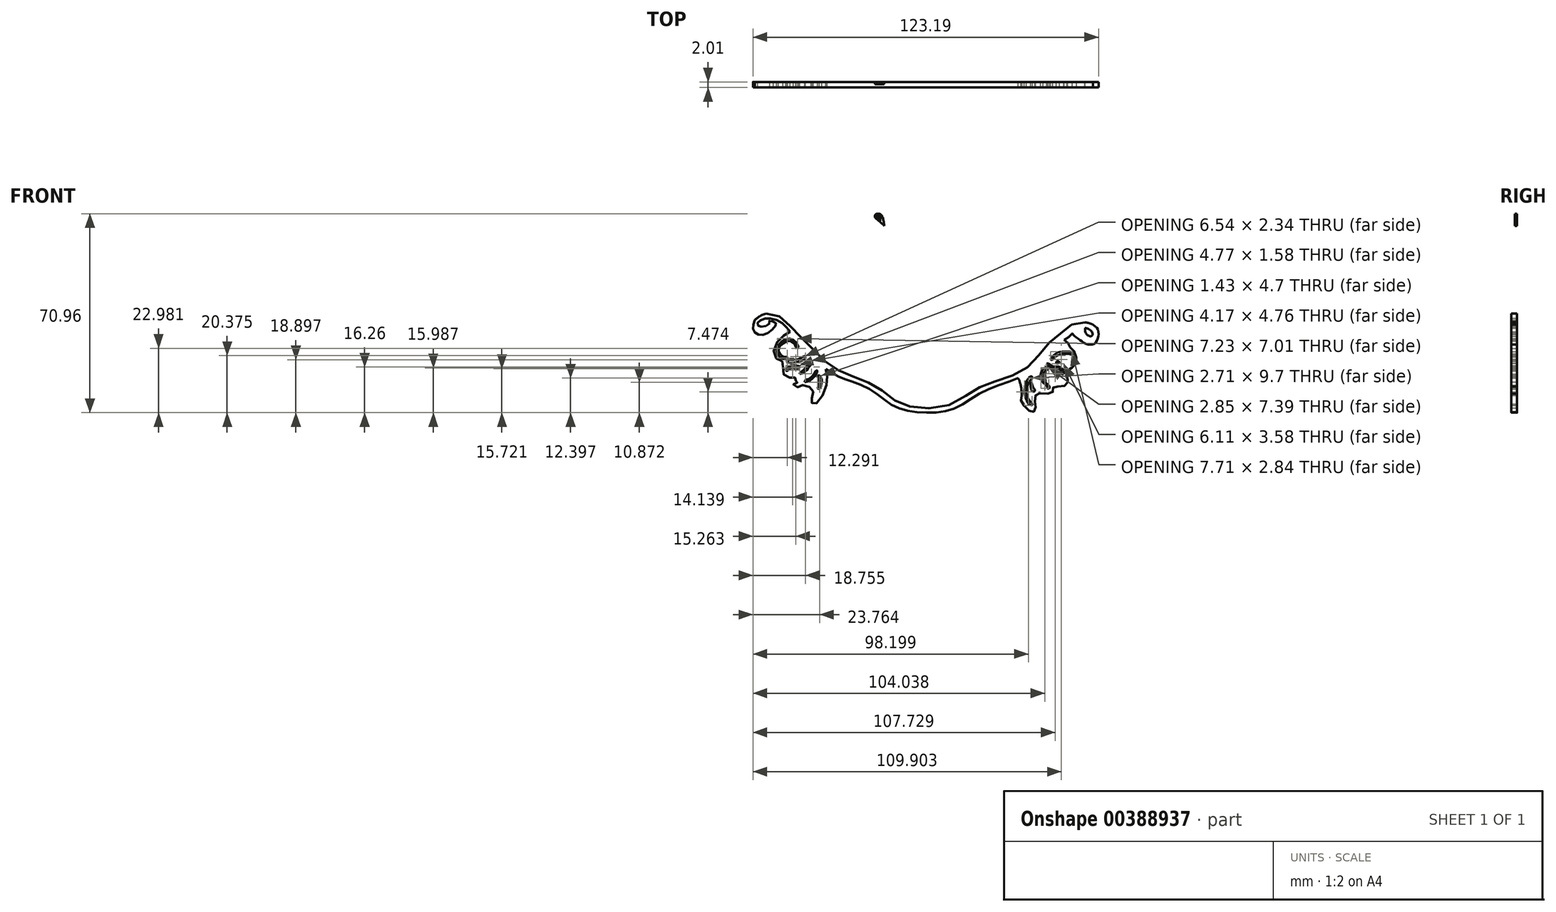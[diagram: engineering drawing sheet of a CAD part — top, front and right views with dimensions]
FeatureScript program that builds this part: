
annotation { "Feature Type Name" : "Feature", "Feature Type Description" : "" }
export const myFeature = defineFeature(function(context is Context, id is Id, definition is map)
    precondition{}
    {
        {
            var Q0;
            Q0=qCreatedBy(makeId("Front.planeOp"),FACE);
            var sketch = newSketch(context, id + "F0", { "sketchPlane" : qUnion([Q0])});
            skFitSpline(sketch, "E0", {"points": [v(-19.06, -22.64) * mm, v(-20.05, -23.28) * mm, v(-21.17, -24.66) * mm, v(-21.14, -26.1) * mm, v(-20.24, -26.68) * mm, v(-20.05, -26.78) * mm, v(-20.05, -28.02) * mm, v(-19.7, -28.73) * mm, v(-18.72, -28.96) * mm, v(-18.37, -28.92) * mm, v(-18.26, -29) * mm, v(-18.28, -29.36) * mm, v(-18, -29.5) * mm, v(-18.05, -29.57) * mm, v(-18.53, -29.7) * mm, v(-18.56, -30.03) * mm, v(-18.01, -30.22) * mm, v(-17.5, -29.95) * mm, v(-16.56, -30.12) * mm, v(-15.97, -30.64) * mm, v(-16, -31.53) * mm, v(-16.2, -32.1) * mm, v(-16, -32.47) * mm, v(-15.44, -32.4) * mm, v(-14.27, -30.56) * mm, v(-14, -28.79) * mm, v(-14.2, -27.76) * mm], "startDerivative": vector(-19.78, -11.14) * mm, "endDerivative": vector(-5.37, 21.05) * mm});
            skFitSpline(sketch, "E1", {"points": [v(-14.2, -27.76) * mm, v(-16.2, -25.63) * mm, v(-18.24, -23.45) * mm, v(-19.06, -22.64) * mm, v(-20.05, -21.54) * mm, v(-21.57, -20.88) * mm, v(-22.78, -20.92) * mm, v(-23.48, -21.37) * mm, v(-23.5, -21.72) * mm, v(-23.2, -21.93) * mm, v(-22.36, -21.87) * mm, v(-21.9, -21.51) * mm, v(-21.88, -21.16) * mm, v(-21.32, -21.3) * mm, v(-20.95, -21.55) * mm, v(-21.14, -21.94) * mm, v(-22.16, -22.82) * mm, v(-23.15, -23.1) * mm, v(-23.83, -22.82) * mm, v(-24.15, -22.22) * mm, v(-23.98, -21.37) * mm, v(-23.86, -20.47) * mm, v(-24.2, -19.7) * mm, v(-24.66, -19.2) * mm, v(-24.75, -18.9) * mm, v(-24.3, -18.34) * mm, v(-23.08, -17.57) * mm, v(-21.55, -17.56) * mm, v(-19.9, -18.28) * mm, v(-18.3, -19.4) * mm, v(-16.67, -20.86) * mm, v(-15.6, -22.07) * mm, v(-14.1, -23.87) * mm, v(-12.14, -25.56) * mm, v(-10.39, -26.53) * mm, v(-8.44, -27.2) * mm, v(-5.99, -28.28) * mm, v(-4.2, -29.6) * mm, v(-2.28, -30.28) * mm, v(-0.2, -30.3) * mm, v(2.58, -29.54) * mm, v(5.26, -28.2) * mm, v(8.77, -26.78) * mm, v(9.41, -26.65) * mm, v(11.78, -25.36) * mm, v(14.45, -23.04) * mm, v(14.48, -22.64) * mm, v(14.42, -21.53) * mm, v(15.26, -19.72) * mm, v(16.52, -18.65) * mm, v(17.53, -18.57) * mm, v(18.11, -18.9) * mm, v(18.07, -19.55) * mm, v(18, -19.69) * mm, v(18.83, -19.1) * mm, v(20.97, -18.63) * mm, v(22.66, -19.01) * mm, v(23.52, -19.67) * mm, v(23.84, -20.62) * mm, v(23.52, -21.03) * mm, v(23.13, -20.85) * mm, v(22.93, -21.03) * mm, v(22.8, -21.42) * mm, v(22.3, -21.67) * mm, v(22.84, -22.17) * mm, v(23, -23.35) * mm, v(22.47, -24.3) * mm, v(21.3, -24.28) * mm, v(20.25, -23.57) * mm, v(19.46, -22.82) * mm, v(20.12, -22.18) * mm, v(21.2, -22.13) * mm, v(21.96, -22.45) * mm, v(22.24, -23) * mm, v(21.92, -23.27) * mm, v(21.32, -22.82) * mm, v(21.2, -22.14) * mm], "startDerivative": vector(-92.8, 97.5) * mm, "endDerivative": vector(-0.23, 68.35) * mm});
            skLineSegment(sketch, "E2", {"start": v(21.2, -22.14) * mm, "end": v(21.2, -22.13) * mm});
            skFitSpline(sketch, "E3", {"points": [v(19.46, -22.82) * mm, v(19.39, -22.99) * mm, v(18.36, -23.75) * mm, v(17.08, -24.5) * mm, v(16.07, -25.85) * mm, v(13.94, -27.93) * mm, v(11.12, -29.36) * mm, v(7.1, -30.91) * mm, v(3.97, -32.85) * mm, v(0.94, -33.67) * mm, v(-2.51, -33.52) * mm, v(-5.24, -32.64) * mm, v(-7.54, -30.9) * mm, v(-10.64, -29.44) * mm, v(-12.46, -28.79) * mm, v(-14.2, -27.76) * mm], "startDerivative": vector(-1.63, -7.8) * mm, "endDerivative": vector(-28.62, 18.77) * mm});
            skFitSpline(sketch, "E4", {"points": [v(12.8, -28.63) * mm, v(12.8, -30.04) * mm, v(12.55, -31.33) * mm, v(12.47, -32.12) * mm, v(13.23, -33.09) * mm, v(14.06, -33.65) * mm, v(14.44, -33.2) * mm, v(14.39, -32.3) * mm, v(14.47, -31.3) * mm, v(15, -31.06) * mm, v(16.65, -31.04) * mm, v(16.82, -30.58) * mm, v(16.9, -30.2) * mm, v(18.08, -30.12) * mm, v(18.76, -29.77) * mm, v(18.78, -28.63) * mm, v(18.78, -27.94) * mm, v(19.62, -27.42) * mm, v(20.03, -26.64) * mm, v(19.84, -25.5) * mm, v(19.22, -24.8) * mm, v(18.95, -24.27) * mm, v(18.36, -23.75) * mm], "startDerivative": vector(-7.26, -31.01) * mm, "endDerivative": vector(-16.3, 11.39) * mm});
            skFitSpline(sketch, "E5", {"points": [v(-14.2, -27.76) * mm, v(-16.2, -25.63) * mm, v(-18.24, -23.45) * mm, v(-19.06, -22.64) * mm, v(-20.05, -21.54) * mm, v(-21.57, -20.88) * mm, v(-22.78, -20.92) * mm, v(-23.48, -21.37) * mm, v(-23.5, -21.72) * mm, v(-23.2, -21.93) * mm, v(-22.36, -21.87) * mm, v(-21.9, -21.51) * mm, v(-21.88, -21.16) * mm, v(-21.32, -21.3) * mm, v(-20.95, -21.55) * mm, v(-21.14, -21.94) * mm, v(-22.16, -22.82) * mm, v(-23.15, -23.1) * mm, v(-23.83, -22.82) * mm, v(-24.15, -22.22) * mm, v(-23.98, -21.37) * mm, v(-23.86, -20.47) * mm, v(-24.2, -19.7) * mm, v(-24.66, -19.2) * mm, v(-24.75, -18.9) * mm, v(-24.3, -18.34) * mm, v(-23.08, -17.57) * mm, v(-21.55, -17.56) * mm, v(-19.9, -18.28) * mm, v(-18.3, -19.4) * mm, v(-16.67, -20.86) * mm, v(-15.6, -22.07) * mm, v(-14.1, -23.87) * mm, v(-12.14, -25.56) * mm, v(-10.39, -26.53) * mm, v(-8.44, -27.2) * mm, v(-5.99, -28.28) * mm, v(-4.2, -29.6) * mm, v(-2.28, -30.28) * mm, v(-0.2, -30.3) * mm, v(2.58, -29.54) * mm, v(5.26, -28.2) * mm, v(8.77, -26.78) * mm, v(9.41, -26.65) * mm, v(11.78, -25.36) * mm, v(14.45, -23.04) * mm, v(14.48, -22.64) * mm, v(14.42, -21.53) * mm, v(15.26, -19.72) * mm, v(16.52, -18.65) * mm, v(17.53, -18.57) * mm, v(18.11, -18.9) * mm, v(18.07, -19.55) * mm, v(18, -19.69) * mm, v(18.83, -19.1) * mm, v(20.97, -18.63) * mm, v(22.66, -19.01) * mm, v(23.52, -19.67) * mm, v(23.84, -20.62) * mm, v(23.52, -21.03) * mm, v(23.13, -20.85) * mm, v(22.93, -21.03) * mm, v(22.8, -21.42) * mm, v(22.3, -21.67) * mm, v(22.84, -22.17) * mm, v(23, -23.35) * mm, v(22.47, -24.3) * mm, v(21.3, -24.28) * mm, v(20.25, -23.57) * mm, v(19.46, -22.82) * mm, v(20.12, -22.18) * mm, v(21.2, -22.13) * mm, v(21.96, -22.45) * mm, v(22.24, -23) * mm, v(21.92, -23.27) * mm, v(21.32, -22.82) * mm, v(21.2, -22.14) * mm], "startDerivative": vector(-92.8, 97.5) * mm, "endDerivative": vector(-0.23, 68.35) * mm});
            skFitSpline(sketch, "E6", {"points": [v(-19.05, -18.84) * mm, v(-19.5, -18.2) * mm, v(-19.43, -17.39) * mm, v(-18.26, -17.03) * mm, v(-17.3, -17.47) * mm, v(-16.59, -19) * mm, v(-16.24, -21.32) * mm], "startDerivative": vector(-4.14, 4.31) * mm, "endDerivative": vector(1.1, -10.49) * mm});
            skFitSpline(sketch, "E7", {"points": [v(-19.52, -26.08) * mm, v(-19.84, -26.12) * mm, v(-20.45, -25.73) * mm, v(-20.62, -24.86) * mm, v(-19.83, -24.09) * mm, v(-19.21, -23.9) * mm, v(-18.43, -24.31) * mm, v(-18.22, -24.88) * mm, v(-17.97, -24.91) * mm, v(-17.96, -24.62) * mm, v(-18.36, -24) * mm, v(-19.05, -23.59) * mm, v(-19.74, -23.69) * mm, v(-20.73, -24.56) * mm, v(-20.88, -25.38) * mm, v(-20.47, -26.16) * mm, v(-19.75, -26.41) * mm, v(-19.4, -26.3) * mm, v(-19.52, -26.08) * mm]});
            skFitSpline(sketch, "E8", {"points": [v(-19.55, -26.72) * mm, v(-19.34, -26.54) * mm, v(-18.47, -26.48) * mm, v(-17.55, -26.2) * mm, v(-17.08, -26) * mm, v(-17.01, -26.3) * mm, v(-18.24, -26.82) * mm, v(-19.24, -26.9) * mm, v(-19.55, -26.72) * mm]});
            skFitSpline(sketch, "E9", {"points": [v(-19.65, -27.89) * mm, v(-19.49, -27.99) * mm, v(-19.17, -27.73) * mm, v(-18.62, -27.6) * mm, v(-18.01, -27.68) * mm, v(-17.79, -27.48) * mm, v(-17.94, -27.3) * mm, v(-19.05, -27.33) * mm, v(-19.48, -27.6) * mm, v(-19.65, -27.89) * mm]});
            skFitSpline(sketch, "E10", {"points": [v(-17.76, -28.4) * mm, v(-17.68, -28.21) * mm, v(-17.17, -27.82) * mm, v(-16.63, -27.06) * mm, v(-16.24, -26.57) * mm, v(-16.07, -26.72) * mm, v(-16.55, -27.58) * mm, v(-17.22, -28.25) * mm, v(-17.76, -28.4) * mm]});
            skFitSpline(sketch, "E11", {"points": [v(-17.05, -29.5) * mm, v(-17.02, -29.33) * mm, v(-16.45, -29.05) * mm, v(-15.89, -28.5) * mm, v(-15.57, -28.01) * mm, v(-15.36, -27.96) * mm, v(-15.45, -28.3) * mm, v(-16.03, -29.05) * mm, v(-16.71, -29.46) * mm, v(-17.05, -29.5) * mm]});
            skFitSpline(sketch, "E12", {"points": [v(-15.32, -28.73) * mm, v(-15.14, -29.09) * mm, v(-15.1, -29.6) * mm, v(-15.25, -30.16) * mm, v(-15.3, -30.4) * mm, v(-15.08, -30.43) * mm, v(-14.74, -29.55) * mm, v(-14.93, -28.73) * mm, v(-15.17, -28.61) * mm, v(-15.32, -28.73) * mm]});
            skFitSpline(sketch, "E13", {"points": [v(-18.46, -17.58) * mm, v(-18.7, -17.6) * mm, v(-18.73, -17.92) * mm, v(-18.26, -17.98) * mm, v(-17.78, -17.9) * mm, v(-17.4, -18.3) * mm, v(-17.53, -18.75) * mm, v(-17.88, -18.95) * mm, v(-17.56, -19.27) * mm, v(-17.57, -19.55) * mm, v(-17.96, -19.36) * mm, v(-18.33, -18.9) * mm, v(-18.05, -18.5) * mm, v(-17.62, -18.4) * mm, v(-17.82, -18.14) * mm, v(-18.34, -18.2) * mm, v(-18.89, -18.1) * mm, v(-19.05, -17.65) * mm, v(-18.66, -17.32) * mm, v(-18.46, -17.58) * mm]});
            skLineSegment(sketch, "E14", {"start": v(18, -19.69) * mm, "end": v(18, -19.69) * mm});
            skFitSpline(sketch, "E15", {"points": [v(13.83, -32.7) * mm, v(13.12, -31.76) * mm, v(12.93, -30.48) * mm, v(13.29, -29.28) * mm, v(13.9, -28.73) * mm, v(14.01, -28.93) * mm, v(13.6, -29.47) * mm, v(13.23, -30.5) * mm, v(13.3, -31.44) * mm, v(13.83, -32.3) * mm, v(14.04, -32.57) * mm, v(13.83, -32.7) * mm]});
            skFitSpline(sketch, "E16", {"points": [v(13.83, -29.51) * mm, v(14.04, -30.01) * mm, v(14.2, -30.37) * mm, v(14.4, -30.67) * mm, v(14.14, -30.85) * mm, v(13.8, -30.24) * mm, v(13.83, -29.51) * mm]});
            skFitSpline(sketch, "E17", {"points": [v(15.63, -27.68) * mm, v(15.89, -27.43) * mm, v(16.08, -27.45) * mm, v(16.14, -27.73) * mm, v(15.77, -28) * mm, v(15.5, -28.55) * mm, v(15.58, -29.26) * mm, v(16.14, -29.88) * mm, v(16.39, -30.25) * mm, v(16.24, -30.46) * mm, v(16.04, -30.16) * mm, v(15.4, -29.5) * mm, v(15.17, -28.81) * mm, v(15.27, -28.04) * mm, v(15.63, -27.68) * mm]});
            skFitSpline(sketch, "E18", {"points": [v(15.96, -27) * mm, v(16.55, -27.56) * mm, v(17.47, -27.7) * mm, v(17.84, -27.87) * mm, v(17.9, -28.19) * mm, v(18.02, -28.43) * mm, v(18.28, -28.4) * mm, v(18.25, -27.99) * mm, v(17.82, -27.49) * mm, v(17.21, -27.4) * mm, v(16.72, -27.35) * mm, v(16.27, -27.02) * mm, v(15.96, -27) * mm]});
            skFitSpline(sketch, "E19", {"points": [v(16.48, -26.45) * mm, v(16.71, -26.5) * mm, v(17, -26.18) * mm, v(17.64, -25.79) * mm, v(18.56, -25.67) * mm, v(19.17, -25.74) * mm, v(19.45, -25.78) * mm, v(19.35, -25.48) * mm, v(18.57, -25.36) * mm, v(17.74, -25.4) * mm, v(17.09, -25.75) * mm, v(16.48, -26.45) * mm]});
            skFitSpline(sketch, "E20", {"points": [v(17.33, -26.7) * mm, v(17.59, -26.7) * mm, v(17.7, -26.87) * mm, v(17.32, -26.98) * mm, v(17.33, -26.7) * mm]});
            skFitSpline(sketch, "E21", {"points": [v(-24.2, -19.7) * mm, v(-23.24, -19.01) * mm, v(-21.57, -18.66) * mm, v(-18.66, -19.7) * mm, v(-16.53, -21.65) * mm, v(-13.34, -25.43) * mm, v(-10.24, -27.16) * mm, v(-6.98, -28.29) * mm, v(-4.8, -29.96) * mm, v(-2.31, -31.01) * mm, v(0.92, -30.9) * mm, v(5.21, -28.91) * mm, v(9.74, -27.21) * mm, v(12.85, -25.19) * mm, v(15.61, -22.58) * mm, v(18, -20.43) * mm, v(20.89, -19.37) * mm, v(22.62, -19.7) * mm, v(23.13, -20.85) * mm], "startDerivative": vector(25.16, 21.25) * mm, "endDerivative": vector(8.41, -36.63) * mm});
            skFitSpline(sketch, "E22", {"points": [v(-22.66, -18.77) * mm, v(-22.36, -20.18) * mm], "startDerivative": vector(1.52, -1.33) * mm, "endDerivative": vector(-0.17, -1.57) * mm});
            skLineSegment(sketch, "E23", {"start": v(-22.36, -20.18) * mm, "end": v(-22.36, -20.18) * mm});
            skFitSpline(sketch, "E24", {"points": [v(-23.9, -21.05) * mm, v(-22.36, -20.18) * mm, v(-20.34, -20.66) * mm, v(-18.76, -22.25) * mm, v(-16.8, -24.15) * mm, v(-14.44, -26.57) * mm, v(-12.16, -28.08) * mm, v(-9.34, -29.2) * mm, v(-6.87, -30.42) * mm, v(-4.65, -32.09) * mm, v(-1.73, -33.02) * mm, v(2.7, -32.66) * mm, v(5.87, -30.77) * mm, v(8.2, -29.65) * mm, v(11.78, -28.42) * mm, v(14.18, -26.72) * mm, v(16.07, -24.38) * mm, v(17.93, -22.87) * mm, v(19.66, -21.54) * mm, v(21.44, -21.4) * mm, v(22.3, -21.67) * mm], "startDerivative": vector(35.8, 29.6) * mm, "endDerivative": vector(25.95, -10.53) * mm});
            skLineSegment(sketch, "E25", {"start": v(21.15, -21.36) * mm, "end": v(21.15, -21.36) * mm});
            skLineSegment(sketch, "E26", {"start": v(22.62, -19.7) * mm, "end": v(22.62, -19.7) * mm});
            skFitSpline(sketch, "E27", {"points": [v(21.15, -21.36) * mm, v(21.85, -20.87) * mm, v(21.84, -20.28) * mm, v(22.62, -19.7) * mm], "startDerivative": vector(2.76, 1.2) * mm, "endDerivative": vector(2.9, 1.39) * mm});
            skFitSpline(sketch, "E28", {"points": [v(18, -19.69) * mm, v(17.38, -20.16) * mm, v(16.31, -20.28) * mm, v(16.03, -19.69) * mm, v(16.41, -19.08) * mm, v(16.97, -18.88) * mm, v(17.14, -19.06) * mm, v(16.79, -19.28) * mm, v(16.5, -19.37) * mm, v(16.43, -19.69) * mm, v(16.98, -19.85) * mm, v(17.57, -19.4) * mm, v(17.56, -18.94) * mm, v(17.53, -18.57) * mm], "startDerivative": vector(-5.6, -5.57) * mm, "endDerivative": vector(-3.88, 1.43) * mm});
            skFitSpline(sketch, "E29", {"points": [v(-14.2, -27.76) * mm, v(-16.2, -25.63) * mm, v(-18.24, -23.45) * mm, v(-19.06, -22.64) * mm, v(-20.05, -21.54) * mm, v(-21.57, -20.88) * mm, v(-22.78, -20.92) * mm, v(-23.48, -21.37) * mm, v(-23.5, -21.72) * mm, v(-23.2, -21.93) * mm, v(-22.36, -21.87) * mm, v(-21.9, -21.51) * mm, v(-21.88, -21.16) * mm, v(-21.32, -21.3) * mm, v(-20.95, -21.55) * mm, v(-21.14, -21.94) * mm, v(-22.16, -22.82) * mm, v(-23.15, -23.1) * mm, v(-23.83, -22.82) * mm, v(-24.15, -22.22) * mm, v(-23.98, -21.37) * mm, v(-23.86, -20.47) * mm, v(-24.2, -19.7) * mm, v(-24.66, -19.2) * mm, v(-24.75, -18.9) * mm, v(-24.3, -18.34) * mm, v(-23.08, -17.57) * mm, v(-21.55, -17.56) * mm, v(-19.9, -18.28) * mm, v(-18.3, -19.4) * mm, v(-16.67, -20.86) * mm, v(-15.6, -22.07) * mm, v(-14.1, -23.87) * mm, v(-12.14, -25.56) * mm, v(-10.39, -26.53) * mm, v(-8.44, -27.2) * mm, v(-5.99, -28.28) * mm, v(-4.2, -29.6) * mm, v(-2.28, -30.28) * mm, v(-0.2, -30.3) * mm, v(2.58, -29.54) * mm, v(5.26, -28.2) * mm, v(8.77, -26.78) * mm, v(9.41, -26.65) * mm, v(11.78, -25.36) * mm, v(14.45, -23.04) * mm, v(14.48, -22.64) * mm, v(14.42, -21.53) * mm, v(15.26, -19.72) * mm, v(16.52, -18.65) * mm, v(17.53, -18.57) * mm, v(18.11, -18.9) * mm, v(18.07, -19.55) * mm, v(18, -19.69) * mm, v(18.83, -19.1) * mm, v(20.97, -18.63) * mm, v(22.66, -19.01) * mm, v(23.52, -19.67) * mm, v(23.84, -20.62) * mm, v(23.52, -21.03) * mm, v(23.13, -20.85) * mm, v(22.93, -21.03) * mm, v(22.8, -21.42) * mm, v(22.3, -21.67) * mm, v(22.84, -22.17) * mm, v(23, -23.35) * mm, v(22.47, -24.3) * mm, v(21.3, -24.28) * mm, v(20.25, -23.57) * mm, v(19.46, -22.82) * mm, v(20.12, -22.18) * mm, v(21.2, -22.13) * mm, v(21.96, -22.45) * mm, v(22.24, -23) * mm, v(21.92, -23.27) * mm, v(21.32, -22.82) * mm, v(21.2, -22.14) * mm], "startDerivative": vector(-92.8, 97.5) * mm, "endDerivative": vector(-0.23, 68.35) * mm});
            skFitSpline(sketch, "E30", {"points": [v(12.55, -31.33) * mm, v(12.07, -28.98) * mm, v(12.02, -28.92) * mm], "startDerivative": vector(0.2, 4.13) * mm, "endDerivative": vector(-0.36, 0.18) * mm});
            skSolve(sketch);
        }
        {
            var Q0;
            {var subQ2=sQuery(id+"F0.wireOp",EDGE,"E2");Q0=makeQuery(id+"F0.imprint","IMPRINT",FACE,{"disambiguationData":[TD([[makeQuery(id+"F0.imprint","IMPRINT",EDGE,{"derivedFrom":subQ2}),1.0]])]});}
            var Q1;
            {var subQ1=sQuery(id+"F0.wireOp",EDGE,"965f58c6-a5c5-4b4c-8e1b-f038c6da23b8");Q1=makeQuery(id+"F0.imprint","IMPRINT",FACE,{"disambiguationData":[TD([[makeQuery(id+"F0.imprint","IMPRINT",EDGE,{"derivedFrom":subQ1}),1.0]])]});}
            extrude(context, id + "F1", {"entities" : qUnion([Q0, Q1]), "depth" : 0.77 * mm});
        }
        {
            var Q0;
            {var subQ2=sQuery(id+"F0.wireOp",EDGE,"965f58c6-a5c5-4b4c-8e1b-f038c6da23b8");Q0=makeQuery(id+"F0.imprint","IMPRINT",FACE,{"disambiguationData":[TD([[makeQuery(id+"F0.imprint","IMPRINT",EDGE,{"derivedFrom":subQ2}),-1.0]])]});}
            var Q1;
            {var subQ0=sQuery(id+"F0.wireOp",EDGE,"E14");Q1=makeQuery(id+"F0.imprint","IMPRINT",FACE,{"disambiguationData":[TD([[makeQuery(id+"F0.imprint","IMPRINT",EDGE,{"derivedFrom":subQ0}),-1.0]])]});}
            var Q2;
            {var subQ0=sQuery(id+"F0.wireOp",EDGE,"E4");Q2=makeQuery(id+"F0.imprint","IMPRINT",FACE,{"disambiguationData":[TD([[makeQuery(id+"F0.imprint","IMPRINT",EDGE,{"derivedFrom":subQ0}),1.0]])]});}
            var Q3;
            {var subQ1=sQuery(id+"F0.wireOp",EDGE,"E0");Q3=makeQuery(id+"F0.imprint","IMPRINT",FACE,{"disambiguationData":[TD([[makeQuery(id+"F0.imprint","IMPRINT",EDGE,{"derivedFrom":subQ1}),1.0]])]});}
            var Q4;
            Q4=makeQuery(id+"F0.imprint","IMPRINT",FACE,{"disambiguationData":[TD([[makeQuery(id+"F0.imprint","IMPRINT",EDGE,{"derivedFrom":sQuery(id+"F0.wireOp",EDGE,"E1")}),1.0]])]});
            var Q5;
            {var subQ0=sQuery(id+"F0.wireOp",EDGE,"E4");var subQ3=sQuery(id+"F0.wireOp",EDGE,"E30");var subQ5=makeQuery(id+"F0.imprint","INTERSECT",VERTEX,{"derivedFrom":[subQ0,subQ3]});Q5=makeQuery(id+"F0.imprint","IMPRINT",FACE,{"disambiguationData":[TD([[makeQuery(id+"F0.imprint","IMPRINT",EDGE,{"disambiguationData":[TD([[subQ5,-1.0]])],"derivedFrom":subQ3}),-1.0]])]});}
            extrude(context, id + "F2", {"entities" : qUnion([Q0, Q1, Q2, Q3, Q4, Q5]), "operationType" : NewBodyOperationType.ADD, "depth" : 0.77 * mm});
        }
        {
            var Q0;
            Q0=makeQuery(id+"F1.opExtrude","SWEPT_BODY",BODY,{"disambiguationData":[OSD([sQuery(id+"F0.wireOp",EDGE,"E1"),sQuery(id+"F0.wireOp",EDGE,"E2"),sQuery(id+"F0.wireOp",EDGE,"E3"),sQuery(id+"F0.wireOp",EDGE,"E1"),sQuery(id+"F0.wireOp",EDGE,"E3"),sQuery(id+"F0.wireOp",EDGE,"E1"),sQuery(id+"F0.wireOp",EDGE,"E1"),sQuery(id+"F0.wireOp",EDGE,"E5"),sQuery(id+"F0.wireOp",EDGE,"E1"),sQuery(id+"F0.wireOp",EDGE,"E14"),sQuery(id+"F0.wireOp",EDGE,"E21"),sQuery(id+"F0.wireOp",EDGE,"E22"),sQuery(id+"F0.wireOp",EDGE,"E24"),sQuery(id+"F0.wireOp",EDGE,"E27")])]});
            var Q1;
            Q1=qCreatedBy(makeId("Origin.pointOp"),VERTEX);
            transform(context, id + "F3", {"entities" : qUnion([Q0]), "transformType" : TransformType.SCALE_UNIFORMLY, "scale" : 2.6, "scalePoint" : qUnion([Q1]), "makeCopy" : false});
        }
    });
